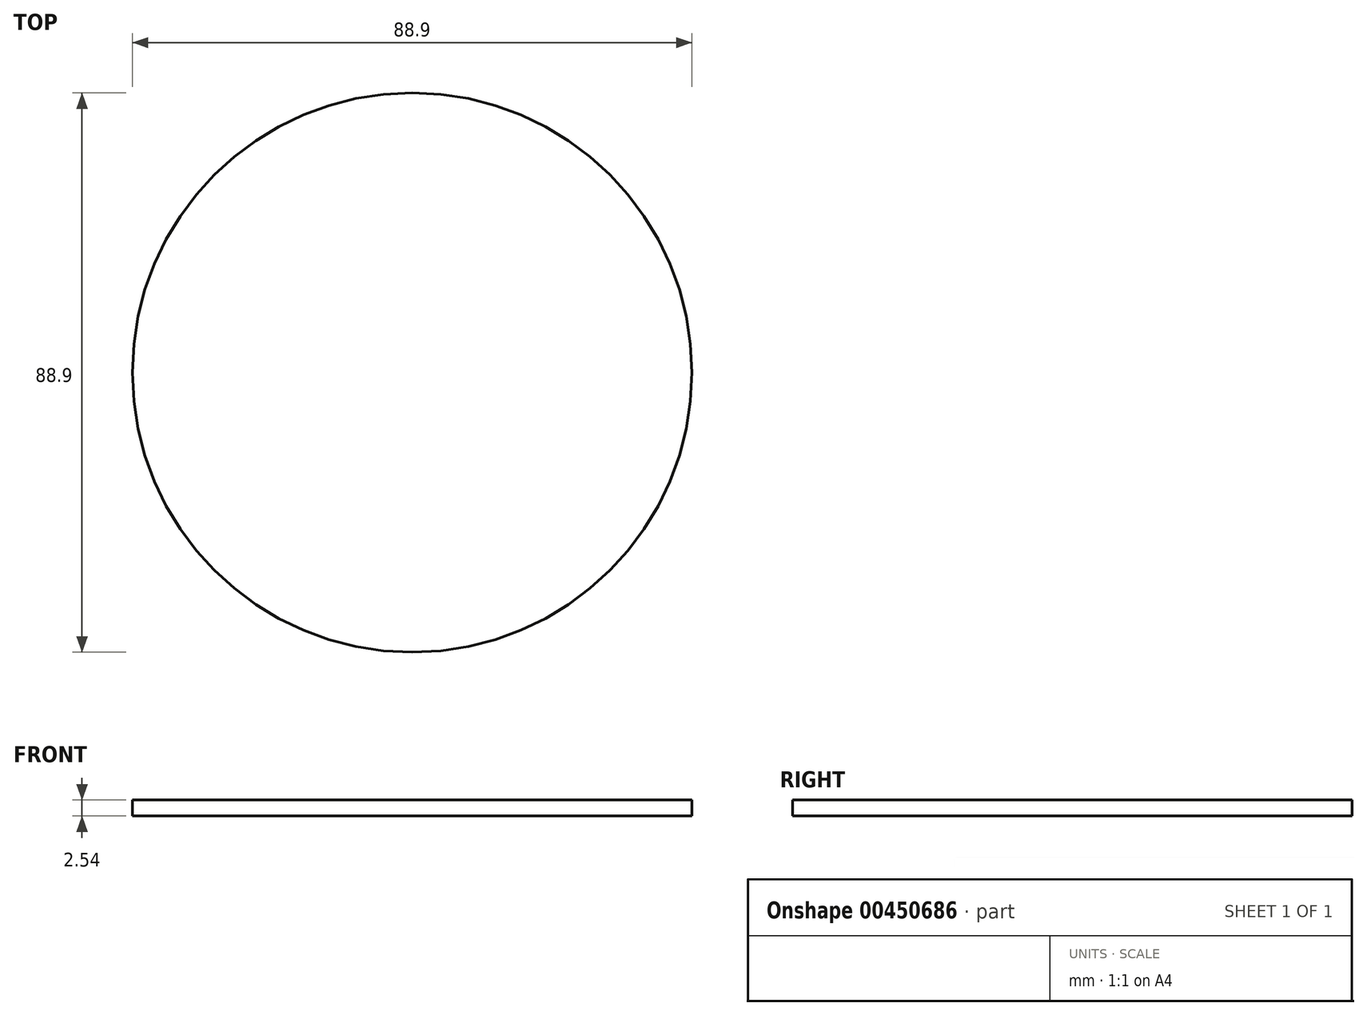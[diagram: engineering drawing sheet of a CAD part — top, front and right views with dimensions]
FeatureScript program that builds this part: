
annotation { "Feature Type Name" : "Feature", "Feature Type Description" : "" }
export const myFeature = defineFeature(function(context is Context, id is Id, definition is map)
    precondition{}
    {
        {
            var Q0;
            Q0=qCreatedBy(makeId("Top.planeOp"),FACE);
            var sketch = newSketch(context, id + "F0", { "sketchPlane" : qUnion([Q0])});
            skCircle(sketch, "E0", {"center": v(0, 0) * mm, "radius": 44.45 * mm});
            skSolve(sketch);
        }
        {
            var Q0;
            Q0=makeQuery(id+"F0.imprint","IMPRINT",FACE,{"disambiguationData":[TD([[makeQuery(id+"F0.imprint","IMPRINT",EDGE,{"derivedFrom":sQuery(id+"F0.wireOp",EDGE,"E0")}),1.0]])]});
            extrude(context, id + "F1", {"entities" : qUnion([Q0]), "depth" : 2.54 * mm});
        }
    });
